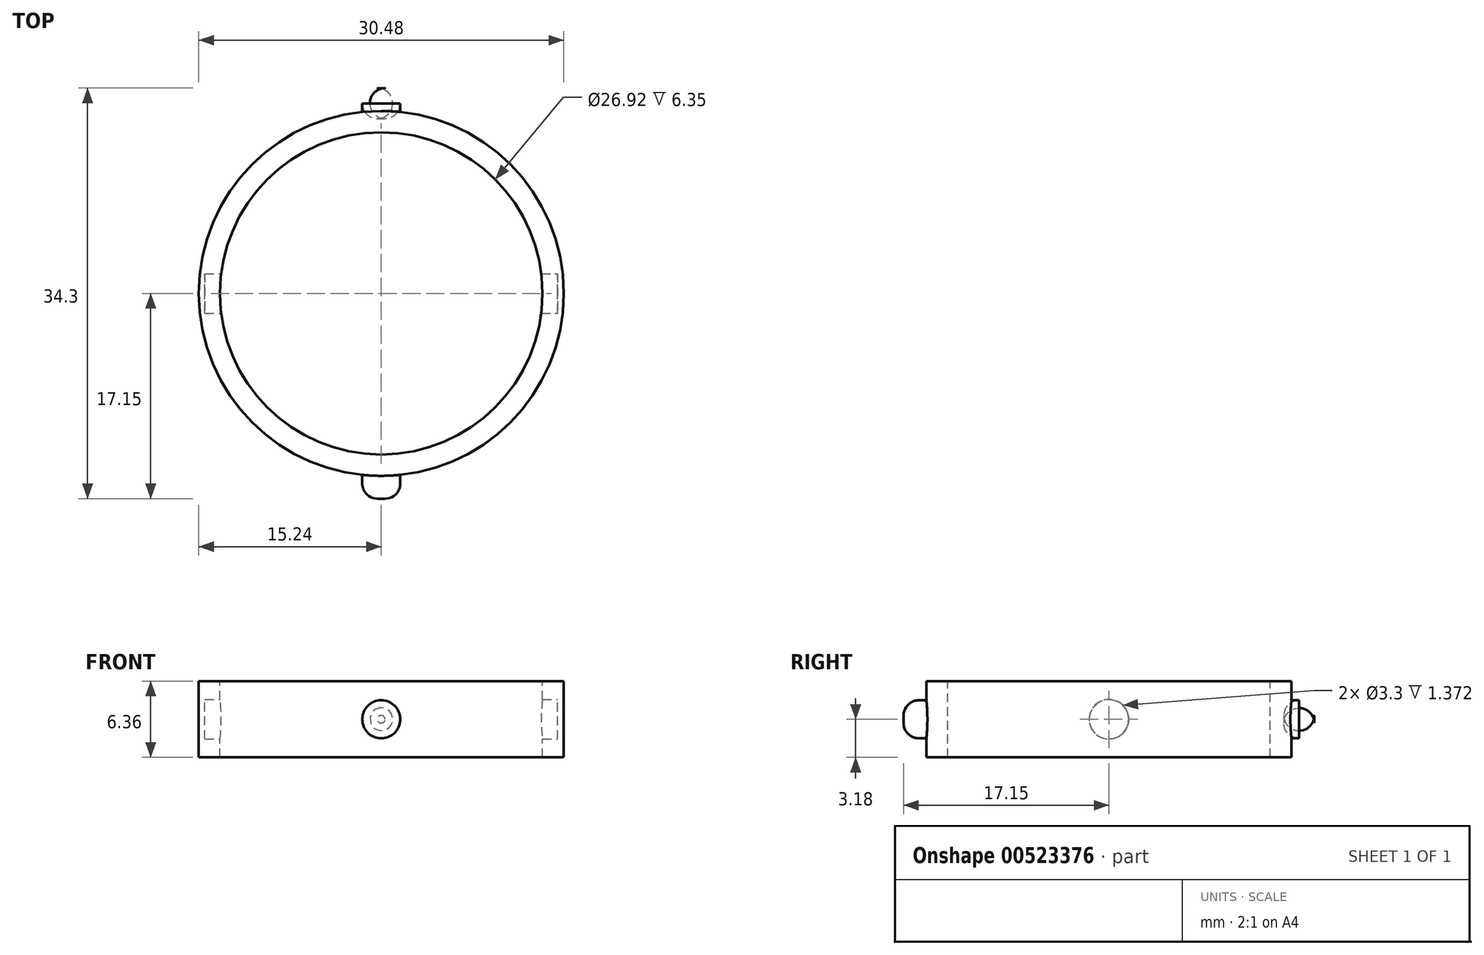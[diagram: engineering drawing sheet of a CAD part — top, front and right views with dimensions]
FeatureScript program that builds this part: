
annotation { "Feature Type Name" : "Feature", "Feature Type Description" : "" }
export const myFeature = defineFeature(function(context is Context, id is Id, definition is map)
    precondition{}
    {
        {
            var Q0;
            Q0=qCreatedBy(makeId("Top.planeOp"),FACE);
            var sketch = newSketch(context, id + "F0", { "sketchPlane" : qUnion([Q0])});
            skCircle(sketch, "E0", {"center": v(0, 0) * mm, "radius": 15.24 * mm});
            skSolve(sketch);
        }
        {
            var Q0;
            Q0=makeQuery(id+"F0.imprint","IMPRINT",FACE,{"disambiguationData":[TD([[makeQuery(id+"F0.imprint","IMPRINT",EDGE,{"derivedFrom":sQuery(id+"F0.wireOp",EDGE,"E0")}),1.0]])]});
            extrude(context, id + "F1", {"entities" : qUnion([Q0]), "endBound" : BoundingType.SYMMETRIC, "depth" : 6.35 * mm, "offsetDistance" : 25.4 * mm});
        }
        {
            var Q0;
            Q0=qCreatedBy(makeId("Right.planeOp"),FACE);
            var sketch = newSketch(context, id + "F2", { "sketchPlane" : qUnion([Q0])});
            skCircle(sketch, "E1", {"center": v(0, 0) * mm, "radius": 1.65 * mm});
            skSolve(sketch);
        }
        {
            var Q0;
            Q0=makeQuery(id+"F2.imprint","IMPRINT",FACE,{"disambiguationData":[TD([[makeQuery(id+"F2.imprint","IMPRINT",EDGE,{"derivedFrom":sQuery(id+"F2.wireOp",EDGE,"E1")}),1.0]])]});
            extrude(context, id + "F3", {"entities" : qUnion([Q0]), "operationType" : NewBodyOperationType.REMOVE, "oppositeDirection" : true, "depth" : 14.73 * mm, "offsetDistance" : 25.4 * mm, "hasSecondDirection" : true, "secondDirectionOppositeDirection" : false, "secondDirectionDepth" : 14.73 * mm});
        }
        {
            var Q0;
            Q0=qCreatedBy(makeId("Front.planeOp"),FACE);
            var sketch = newSketch(context, id + "F4", { "sketchPlane" : qUnion([Q0])});
            skCircle(sketch, "E2", {"center": v(0, 0) * mm, "radius": 1.59 * mm});
            skSolve(sketch);
        }
        {
            var Q0;
            Q0=qSketchRegion(id+"F4",true);
            extrude(context, id + "F5", {"entities" : qUnion([Q0]), "operationType" : NewBodyOperationType.ADD, "endBound" : BoundingType.SYMMETRIC, "depth" : 34.3 * mm, "offsetDistance" : 25.4 * mm});
        }
        {
            var Q0;
            Q0=makeQuery(id+"F1.opExtrude","CAP_FACE",FACE,{"disambiguationData":[OSD([sQuery(id+"F0.wireOp",EDGE,"E0")])],"isStart":false});
            var sketch = newSketch(context, id + "F6", { "sketchPlane" : qUnion([Q0])});
            skCircle(sketch, "E3", {"center": v(0, 0) * mm, "radius": 13.46 * mm});
            skSolve(sketch);
        }
        {
            var Q0;
            Q0=qSketchRegion(id+"F6",true);
            extrude(context, id + "F7", {"entities" : qUnion([Q0]), "operationType" : NewBodyOperationType.REMOVE, "endBound" : BoundingType.THROUGH_ALL, "oppositeDirection" : true, "depth" : 25.4 * mm, "offsetDistance" : 25.4 * mm});
        }
        {
            var Q0;
            Q0=makeQuery(id+"F5.opExtrude","CAP_EDGE",EDGE,{"disambiguationData":[OSD([sQuery(id+"F4.wireOp",EDGE,"E2")])],"isStart":false});
            var Q1;
            Q1=makeQuery(id+"F5.opExtrude","CAP_EDGE",EDGE,{"disambiguationData":[OSD([sQuery(id+"F4.wireOp",EDGE,"E2")])],"isStart":true});
            fillet(context, id + "F8", {"entities" : qUnion([Q0, Q1]), "radius" : 1.27 * mm, "tangentPropagation" : true, "allowEdgeOverflow" : false});
        }
    });
